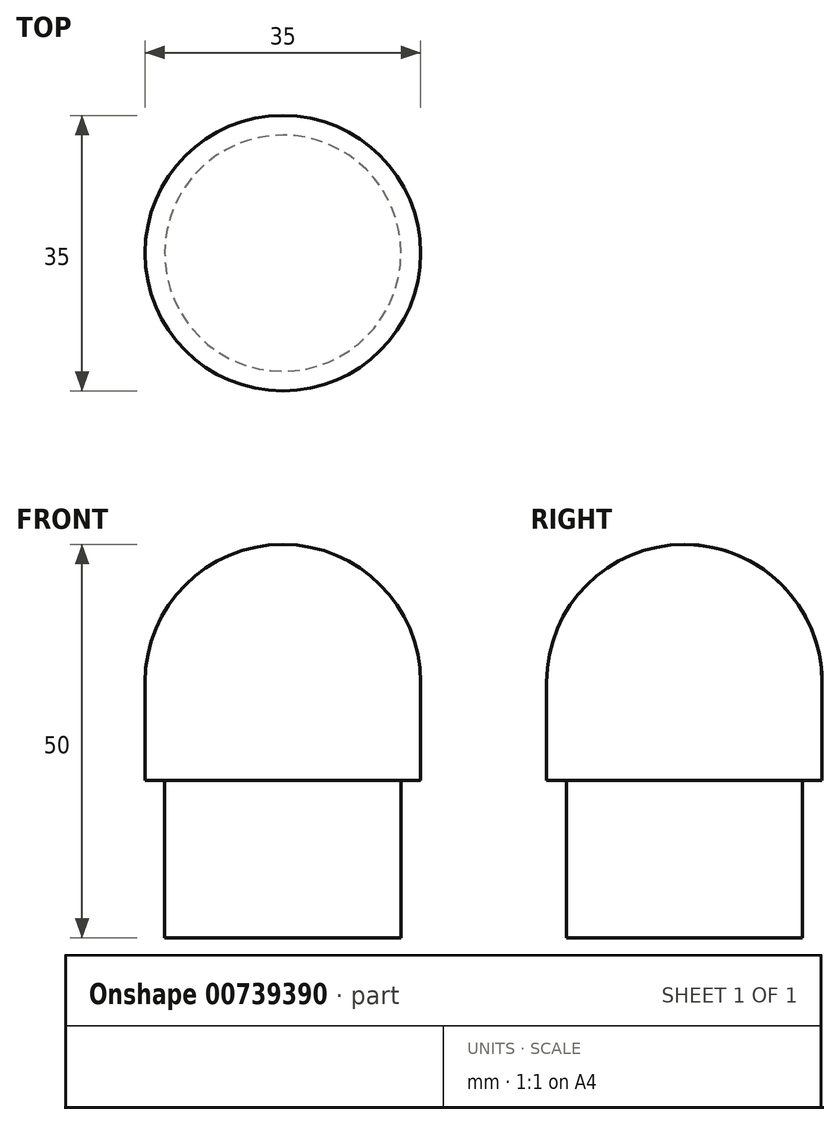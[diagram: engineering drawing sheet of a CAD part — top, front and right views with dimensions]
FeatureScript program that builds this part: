
annotation { "Feature Type Name" : "Feature", "Feature Type Description" : "" }
export const myFeature = defineFeature(function(context is Context, id is Id, definition is map)
    precondition{}
    {
        {
            var Q0;
            Q0=qCreatedBy(makeId("Right.planeOp"),FACE);
            var sketch = newSketch(context, id + "F0", { "sketchPlane" : qUnion([Q0])});
            skLineSegment(sketch, "E0.bottom", {"start": v(0, 0) * mm, "end": v(15, 0) * mm});
            skLineSegment(sketch, "E0.top", {"start": v(0, -20) * mm, "end": v(15, -20) * mm});
            skLineSegment(sketch, "E0.left", {"start": v(0, 0) * mm, "end": v(0, -20) * mm});
            skLineSegment(sketch, "E0.right", {"start": v(15, 0) * mm, "end": v(15, -20) * mm});
            skLineSegment(sketch, "E1.bottom", {"start": v(0, 0) * mm, "end": v(17.5, 0) * mm});
            skLineSegment(sketch, "E1.top", {"start": v(0, 12.5) * mm, "end": v(17.5, 12.5) * mm});
            skLineSegment(sketch, "E1.left", {"start": v(0, 0) * mm, "end": v(0, 12.5) * mm});
            skLineSegment(sketch, "E1.right", {"start": v(17.5, 0) * mm, "end": v(17.5, 12.5) * mm});
            skLineSegment(sketch, "E2", {"start": v(0, -20) * mm, "end": v(0, 30) * mm});
            skArc(sketch, "E3", {"start": v(17.5, 12.5) * mm, "mid": v(12.37, 24.87) * mm, "end": v(0, 30) * mm});
            skSolve(sketch);
        }
        {
            var Q0;
            {var subQ0=sQuery(id+"F0.wireOp",EDGE,"E1.top");Q0=makeQuery(id+"F0.imprint","IMPRINT",FACE,{"disambiguationData":[TD([[makeQuery(id+"F0.imprint","IMPRINT",EDGE,{"derivedFrom":subQ0}),1.0]])]});}
            var Q1;
            {var subQ1=sQuery(id+"F0.wireOp",EDGE,"E1.top");Q1=makeQuery(id+"F0.imprint","IMPRINT",FACE,{"disambiguationData":[TD([[makeQuery(id+"F0.imprint","IMPRINT",EDGE,{"derivedFrom":subQ1}),-1.0]])]});}
            var Q2;
            {var subQ0=sQuery(id+"F0.wireOp",EDGE,"E0.top");Q2=makeQuery(id+"F0.imprint","IMPRINT",FACE,{"disambiguationData":[TD([[makeQuery(id+"F0.imprint","IMPRINT",EDGE,{"derivedFrom":subQ0}),1.0]])]});}
            var Q3;
            Q3=sQuery(id+"F0.wireOp",EDGE,"E2");
            revolve(context, id + "F1", {"surfaceOperationType" : NewSurfaceOperationType.NEW, "entities" : qUnion([Q0, Q1, Q2]), "axis" : qUnion([Q3]), "revolveType" : RevolveType.FULL});
        }
    });
